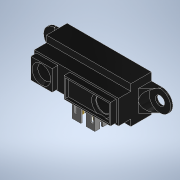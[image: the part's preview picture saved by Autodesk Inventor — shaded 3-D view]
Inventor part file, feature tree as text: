
AUTODESK INVENTOR PART (.ipt)
format: ipt  version: 2022.3 (Build 263350000, 350)  size: 224,768 bytes
history: mixed  units: mm (DEFAULTED — no unit token found)
features: other x4, revolve x2, chamfer x2, imported_body x1
ambient origin geometry x8: Origin, YZ Plane, XZ Plane, XY Plane, X Axis, Y Axis, Z Axis, Center Point
bodies: Solid1 (imported_parasolid), Solid2 (imported_parasolid), Solid3 (imported_parasolid), Solid4 (imported_parasolid), Solid5 (imported_parasolid), Solid6 (imported_parasolid), Solid7 (imported_parasolid), Solid8 (imported_parasolid)
feature tree (9):
  revolve  "Revolve1"  [1 undecoded]
  chamfer  "Chamfer2"  [1 undecoded]
  revolve  "Revolve2"  [1 undecoded]
  other  "Boss-Extrude8"
  other  "Cut-Extrude13"
  chamfer  "Chamfer3"  [1 undecoded]
  other  "LPattern1[1]"
  other  "LPattern1[2]"
  imported_body  NMx_Import_Brep_tag  [imported B-rep: ~47 faces, bbox_mm=[31.95, 15.6, 11.75]]
note: 4 required parameter values undecoded (feature->parameter linkage not recoverable at this tier; creation-order binding heuristic only, values carry confidence <= 0.55)
